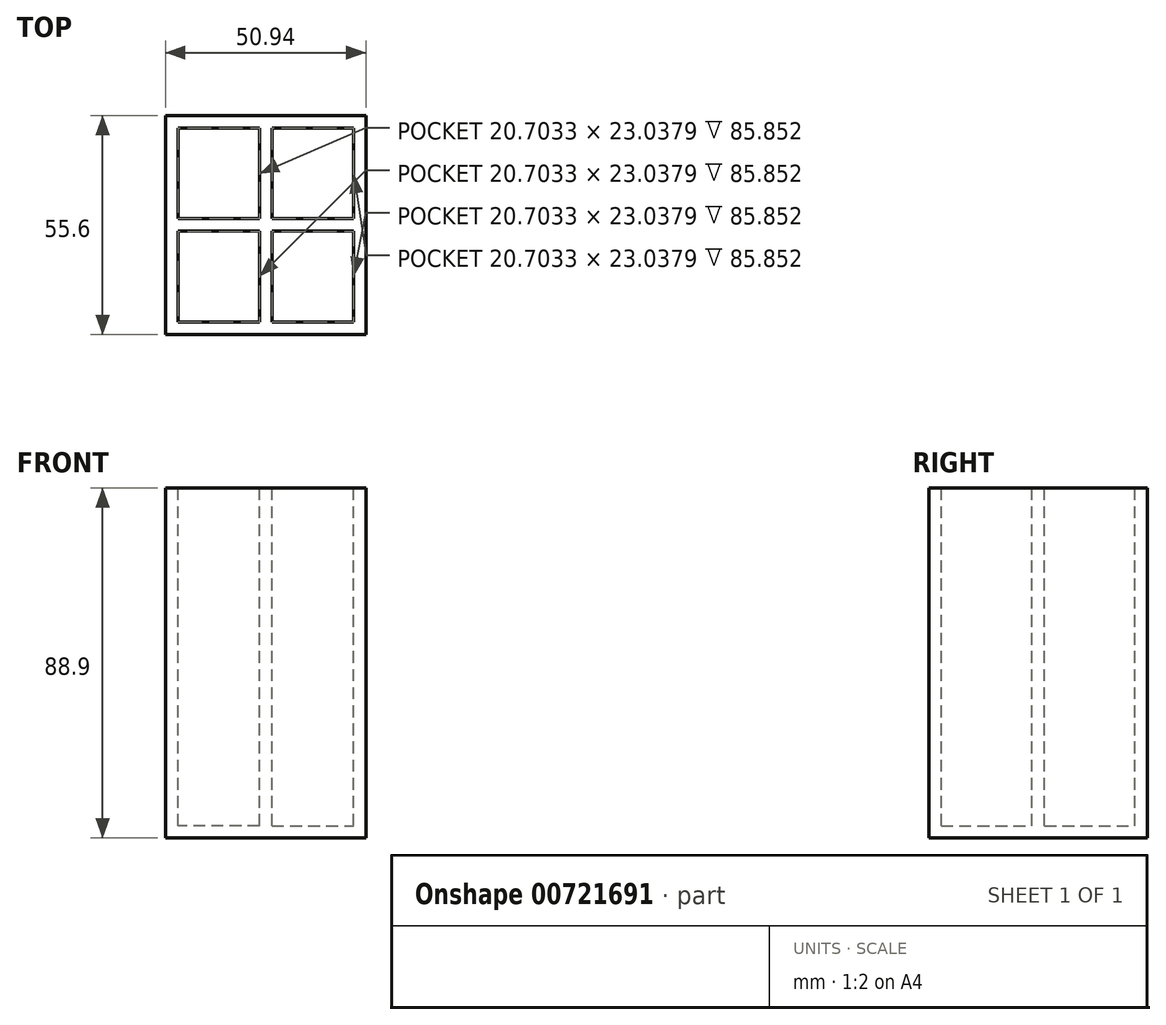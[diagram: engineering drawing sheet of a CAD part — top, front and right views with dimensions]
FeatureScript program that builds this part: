
annotation { "Feature Type Name" : "Feature", "Feature Type Description" : "" }
export const myFeature = defineFeature(function(context is Context, id is Id, definition is map)
    precondition{}
    {
        {
            var Q0;
            Q0=qCreatedBy(makeId("Top.planeOp"),FACE);
            var sketch = newSketch(context, id + "F0", { "sketchPlane" : qUnion([Q0])});
            skLineSegment(sketch, "E0.bottom", {"start": v(25.47, -27.8) * mm, "end": v(-25.47, -27.8) * mm});
            skLineSegment(sketch, "E0.top", {"start": v(25.47, 27.8) * mm, "end": v(-25.47, 27.8) * mm});
            skLineSegment(sketch, "E0.left", {"start": v(25.47, -27.8) * mm, "end": v(25.47, 27.8) * mm});
            skLineSegment(sketch, "E0.right", {"start": v(-25.47, -27.8) * mm, "end": v(-25.47, 27.8) * mm});
            skPoint(sketch, "E0.middle", {"position": v(0, 0) * mm});
            skSolve(sketch);
        }
        {
            var Q0;
            Q0=qSketchRegion(id+"F0",true);
            extrude(context, id + "F1", {"entities" : qUnion([Q0]), "depth" : 88.9 * mm, "offsetDistance" : 25.4 * mm});
        }
        {
            var Q0;
            Q0=makeQuery(id+"F1.opExtrude","CAP_FACE",FACE,{"disambiguationData":[OSD([sQuery(id+"F0.wireOp",EDGE,"E0.bottom"),sQuery(id+"F0.wireOp",EDGE,"E0.top"),sQuery(id+"F0.wireOp",EDGE,"E0.left"),sQuery(id+"F0.wireOp",EDGE,"E0.right")])],"isStart":false});
            var sketch = newSketch(context, id + "F2", { "sketchPlane" : qUnion([Q0])});
            skLineSegment(sketch, "E1", {"start": v(0, 27.8) * mm, "end": v(0, -27.8) * mm});
            skLineSegment(sketch, "E2", {"start": v(-25.47, 0) * mm, "end": v(25.47, 0) * mm});
            skLineSegment(sketch, "E3.right", {"start": v(-22.3, 1.59) * mm, "end": v(-22.3, 23.61) * mm});
            skPoint(sketch, "E3.middle", {"position": v(-10.62, 13.99) * mm});
            skLineSegment(sketch, "E4", {"start": v(0, -27.8) * mm, "end": v(0, 27.8) * mm});
            skLineSegment(sketch, "E5", {"start": v(25.47, 0) * mm, "end": v(-25.47, 0) * mm});
            skPoint(sketch, "E6.middle", {"position": v(16.03, -13.1) * mm});
            skPoint(sketch, "E7.middle", {"position": v(24.21, -20.3) * mm});
            skLineSegment(sketch, "E8.bottom", {"start": v(-1.59, -24.63) * mm, "end": v(-22.3, -24.63) * mm});
            skLineSegment(sketch, "E8.top", {"start": v(-1.59, -1.59) * mm, "end": v(-22.3, -1.59) * mm});
            skLineSegment(sketch, "E8.left", {"start": v(-1.59, -24.63) * mm, "end": v(-1.59, -1.59) * mm});
            skLineSegment(sketch, "E8.right", {"start": v(-22.3, -24.63) * mm, "end": v(-22.3, -1.59) * mm});
            skPoint(sketch, "E8.middle", {"position": v(-11.94, -13.1) * mm});
            skPoint(sketch, "E8.middle.positionSnap0", {"position": v(-11.94, 5.75) * mm});
            skPoint(sketch, "E8.centerSnap0", {"position": v(-11.94, 5.75) * mm});
            skLineSegment(sketch, "E9.bottom", {"start": v(1.59, -1.59) * mm, "end": v(22.3, -1.59) * mm});
            skLineSegment(sketch, "E9.top", {"start": v(1.59, -24.63) * mm, "end": v(22.3, -24.63) * mm});
            skLineSegment(sketch, "E9.left", {"start": v(1.59, -1.59) * mm, "end": v(1.59, -24.63) * mm});
            skLineSegment(sketch, "E9.right", {"start": v(22.3, -1.59) * mm, "end": v(22.3, -24.63) * mm});
            skPoint(sketch, "E9.middle", {"position": v(11.94, -13.1) * mm});
            skLineSegment(sketch, "E10.bottom", {"start": v(-1.59, 1.59) * mm, "end": v(-22.3, 1.59) * mm});
            skLineSegment(sketch, "E10.top", {"start": v(-1.59, 24.63) * mm, "end": v(-20.84, 24.63) * mm});
            skLineSegment(sketch, "E10.left", {"start": v(-1.59, 1.59) * mm, "end": v(-1.59, 24.63) * mm});
            skPoint(sketch, "E10.middle", {"position": v(-11.21, 13.1) * mm});
            skPoint(sketch, "E11.middle", {"position": v(-24.21, 20.3) * mm});
            skLineSegment(sketch, "E12.bottom", {"start": v(1.59, 24.63) * mm, "end": v(22.3, 24.63) * mm});
            skLineSegment(sketch, "E12.top", {"start": v(1.59, 1.59) * mm, "end": v(22.3, 1.59) * mm});
            skLineSegment(sketch, "E12.left", {"start": v(1.59, 24.63) * mm, "end": v(1.59, 1.59) * mm});
            skLineSegment(sketch, "E12.right", {"start": v(22.3, 24.63) * mm, "end": v(22.3, 1.59) * mm});
            skPoint(sketch, "E12.middle", {"position": v(11.94, 13.1) * mm});
            skPoint(sketch, "E12.middle.positionSnap0", {"position": v(11.94, -1.59) * mm});
            skPoint(sketch, "E12.centerSnap0", {"position": v(11.94, -1.59) * mm});
            skPoint(sketch, "E13.orphan", {"position": v(-22.3, 4.36) * mm});
            skPoint(sketch, "E14.orphan", {"position": v(-20.84, 1.59) * mm});
            skPoint(sketch, "E3.left.end.orphan", {"position": v(1.05, 23.61) * mm});
            skPoint(sketch, "E3.left.start.orphan", {"position": v(1.05, 4.36) * mm});
            skLineSegment(sketch, "E15", {"start": v(-20.84, 24.63) * mm, "end": v(-22.3, 24.63) * mm});
            skLineSegment(sketch, "E16", {"start": v(-22.3, 24.63) * mm, "end": v(-22.3, 23.61) * mm});
            skSolve(sketch);
        }
        {
            var Q0;
            Q0=qSketchRegion(id+"F2",true);
            extrude(context, id + "F3", {"entities" : qUnion([Q0]), "operationType" : NewBodyOperationType.REMOVE, "oppositeDirection" : true, "depth" : 85.85 * mm, "offsetDistance" : 25.4 * mm});
        }
    });
